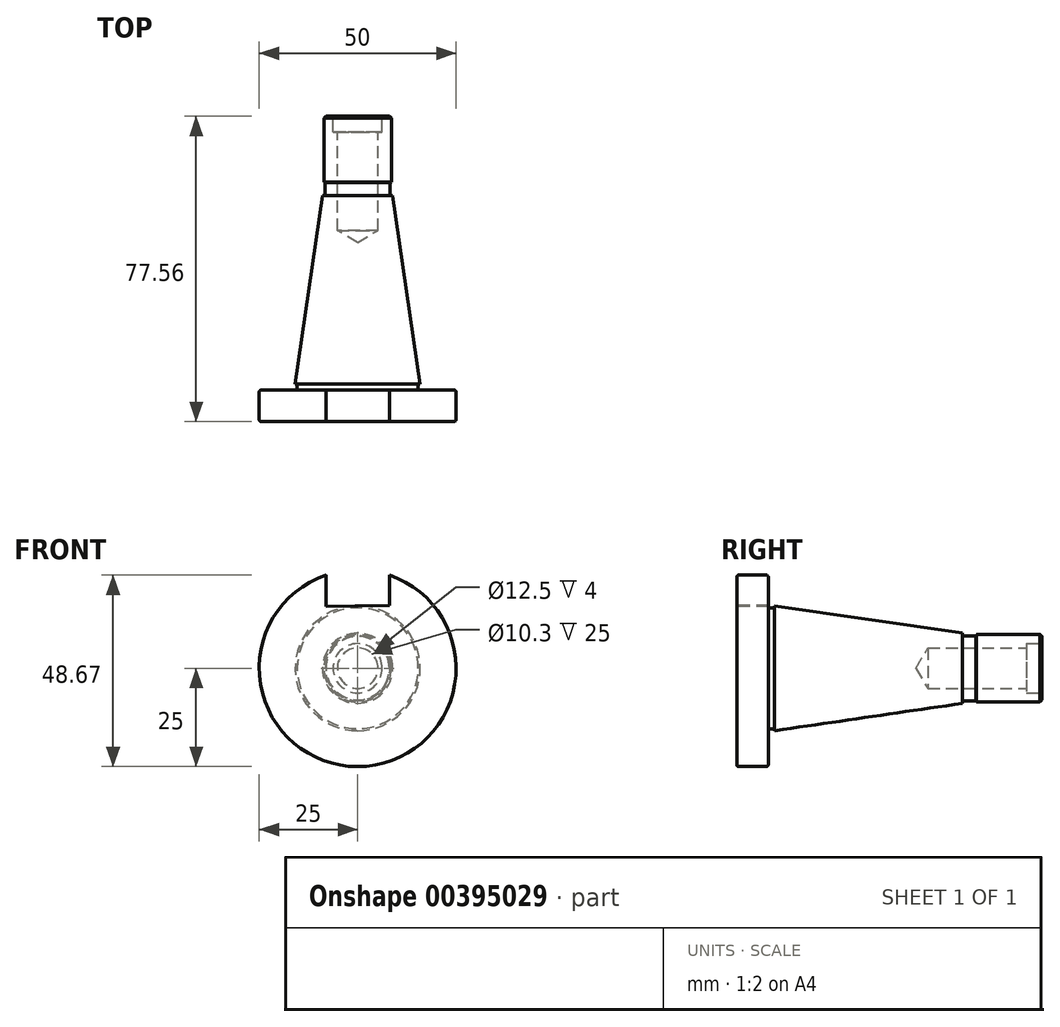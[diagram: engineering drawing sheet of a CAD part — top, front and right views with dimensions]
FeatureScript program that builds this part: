
annotation { "Feature Type Name" : "Feature", "Feature Type Description" : "" }
export const myFeature = defineFeature(function(context is Context, id is Id, definition is map)
    precondition{}
    {
        {
            var Q0;
            Q0=qCreatedBy(makeId("Right.planeOp"),FACE);
            var sketch = newSketch(context, id + "F0", { "sketchPlane" : qUnion([Q0])});
            skLineSegment(sketch, "E0", {"start": v(0, 0) * mm, "end": v(57.36, 0) * mm});
            skLineSegment(sketch, "E1", {"start": v(0, 0) * mm, "end": v(0, 25) * mm});
            skLineSegment(sketch, "E2", {"start": v(0, 25) * mm, "end": v(8, 25) * mm});
            skLineSegment(sketch, "E3", {"start": v(8, 25) * mm, "end": v(8, 15.88) * mm});
            skLineSegment(sketch, "E4", {"start": v(9.6, 15.88) * mm, "end": v(57.36, 8.9) * mm});
            skLineSegment(sketch, "E5", {"start": v(57.36, 8.9) * mm, "end": v(57.36, 0) * mm});
            skLineSegment(sketch, "E6", {"start": v(9.6, 15.88) * mm, "end": v(9.6, 15.38) * mm});
            skLineSegment(sketch, "E7", {"start": v(9.6, 15.38) * mm, "end": v(8, 15.38) * mm});
            skLineSegment(sketch, "E8", {"start": v(8, 15.38) * mm, "end": v(8, 15.88) * mm});
            skSolve(sketch);
        }
        {
            var Q0;
            Q0 = qSketchRegion(id + "F0", true);
            var Q1;
            Q1=sQuery(id+"F0.wireOp",EDGE,"E0");
            revolve(context, id + "F1", {"entities" : qUnion([Q0]), "axis" : qUnion([Q1]), "revolveType" : RevolveType.FULL});
        }
        {
            var Q0;
            Q0=makeQuery(id+"F1.opRevolve","SWEPT_FACE",FACE,{"disambiguationData":[OSD([sQuery(id+"F0.wireOp",EDGE,"E5")])]});
            var sketch = newSketch(context, id + "F2", { "sketchPlane" : qUnion([Q0])});
            skCircle(sketch, "E9", {"center": v(0, 0) * mm, "radius": 8.25 * mm});
            skSolve(sketch);
        }
        {
            var Q0;
            Q0 = qSketchRegion(id + "F2", true);
            extrude(context, id + "F3", {"entities" : qUnion([Q0]), "operationType" : NewBodyOperationType.ADD, "depth" : 3 * mm});
        }
        {
            var Q0;
            Q0=makeQuery(id+"F3.opExtrude","CAP_FACE",FACE,{"disambiguationData":[OSD([sQuery(id+"F2.wireOp",EDGE,"E9")])],"isStart":false});
            var sketch = newSketch(context, id + "F4", { "sketchPlane" : qUnion([Q0])});
            skCircle(sketch, "E10", {"center": v(0, 0) * mm, "radius": 8.55 * mm});
            skSolve(sketch);
        }
        {
            var Q0;
            Q0 = qSketchRegion(id + "F4", true);
            extrude(context, id + "F5", {"entities" : qUnion([Q0]), "operationType" : NewBodyOperationType.ADD, "depth" : 17.2 * mm});
        }
        {
            var Q0;
            Q0=makeQuery(id+"F5.opExtrude","CAP_FACE",FACE,{"disambiguationData":[OSD([sQuery(id+"F4.wireOp",EDGE,"E10")])],"isStart":false});
            var sketch = newSketch(context, id + "F6", { "sketchPlane" : qUnion([Q0])});
            skCircle(sketch, "E11", {"center": v(0, 0) * mm, "radius": 6.25 * mm});
            skSolve(sketch);
        }
        {
            var Q0;
            Q0=makeQuery(id+"F5.opExtrude","CAP_EDGE",EDGE,{"disambiguationData":[OSD([sQuery(id+"F4.wireOp",EDGE,"E10")])],"isStart":true});
            chamfer(context, id + "F7", {"entities" : qUnion([Q0]), "chamferType" : ChamferType.OFFSET_ANGLE, "width" : .5 * mm, "oppositeDirection" : false, "angle" : 75 * degree, "tangentPropagation" : true});
        }
        {
            var Q0;
            Q0 = qSketchRegion(id + "F6", true);
            extrude(context, id + "F8", {"entities" : qUnion([Q0]), "operationType" : NewBodyOperationType.REMOVE, "oppositeDirection" : true, "depth" : 4 * mm});
        }
        {
            var Q0;
            Q0=makeQuery(id+"F8.boolean.opBoolean","COPY",FACE,{"derivedFrom":makeQuery(id+"F8.opExtrude","CAP_FACE",FACE,{"disambiguationData":[OSD([sQuery(id+"F6.wireOp",EDGE,"E11")])],"isStart":false})});
            var sketch = newSketch(context, id + "F9", { "sketchPlane" : qUnion([Q0])});
            skPoint(sketch, "E12", {"position": v(0, 0) * mm});
            skSolve(sketch);
        }
        {
            var Q0;
            Q0=sQuery(id+"F9.wireOp",VERTEX,"E12");
            var Q1;
            Q1=makeQuery(id+"F1.opRevolve","SWEPT_BODY",BODY,{"disambiguationData":[OSD([sQuery(id+"F0.wireOp",EDGE,"E0"),sQuery(id+"F0.wireOp",EDGE,"E1"),sQuery(id+"F0.wireOp",EDGE,"E2"),sQuery(id+"F0.wireOp",EDGE,"E3"),sQuery(id+"F0.wireOp",EDGE,"E4"),sQuery(id+"F0.wireOp",EDGE,"E5")])]});
            hole(context, id + "F10", {"style" : HoleStyle.SIMPLE, "endStyle" : HoleEndStyle.BLIND, "standardTappedOrClearance" : lookupTablePath({ "standard" : "ISO", "engagement" : "75%", "pitch" : "1.75 mm", "size" : "M12", "type" : "Tapped" }), "standardBlindInLast" : lookupTablePath({ "standard" : "ISO", "engagement" : "75%", "pitch" : "1.75 mm", "size" : "M12", "type" : "Tapped" }), "holeDiameter" : 10.3 * mm, "showTappedDepth" : true, "holeDepth" : 25 * mm, "tappedDepth" : 21.5 * mm, "tapClearance" : 2, "locations" : qUnion([Q0]), "scope" : qUnion([Q1]), "majorDiameter" : 12 * mm});
        }
        {
            var Q0;
            Q0=makeQuery(id+"F1.opRevolve","SWEPT_FACE",FACE,{"disambiguationData":[OSD([sQuery(id+"F0.wireOp",EDGE,"E2")])]});
            fillet(context, id + "F11", {"entities" : qUnion([Q0]), "radius" : .5 * mm, "tangentPropagation" : true, "allowEdgeOverflow" : false});
        }
        {
            var Q0;
            Q0=makeQuery(id+"F5.opExtrude","CAP_EDGE",EDGE,{"disambiguationData":[OSD([sQuery(id+"F4.wireOp",EDGE,"E10")])],"isStart":false});
            var Q1;
            Q1=makeQuery(id+"F8.boolean.opBoolean","COPY",EDGE,{"derivedFrom":makeQuery(id+"F8.opExtrude","CAP_EDGE",EDGE,{"disambiguationData":[OSD([sQuery(id+"F6.wireOp",EDGE,"E11")])],"isStart":true})});
            var Q2;
            Q2=makeQuery(id+"F10.hole-0.boolean.opBoolean","COPY",EDGE,{"derivedFrom":makeQuery(id+"F10.hole-0.opRevolve","SWEPT_EDGE",EDGE,{"disambiguationData":[OSD([sQuery(id+"F10.hole-0.sketch.wireOp",EDGE,"core_line_2"),sQuery(id+"F10.hole-0.sketch.wireOp",EDGE,"core_line_3")])]})});
            chamfer(context, id + "F12", {"entities" : qUnion([Q0, Q1, Q2]), "width" : .5 * mm, "tangentPropagation" : true});
        }
        {
            var Q0;
            Q0=makeQuery(id+"F1.opRevolve","SWEPT_FACE",FACE,{"disambiguationData":[OSD([sQuery(id+"F0.wireOp",EDGE,"E1")])]});
            var sketch = newSketch(context, id + "F13", { "sketchPlane" : qUnion([Q0])});
            skCircle(sketch, "E13", {"center": v(0.27, 0) * mm, "radius": 15.88 * mm, "construction": true});
            skLineSegment(sketch, "E14", {"start": v(0, 15.87) * mm, "end": v(-8.05, 15.73) * mm});
            skLineSegment(sketch, "E15", {"start": v(-8.05, 15.73) * mm, "end": v(8.05, 16.01) * mm});
            skLineSegment(sketch, "E16", {"start": v(8.05, 16.01) * mm, "end": v(8.05, 25) * mm});
            skLineSegment(sketch, "E17", {"start": v(8.05, 25) * mm, "end": v(-8.05, 25) * mm});
            skLineSegment(sketch, "E18", {"start": v(-8.05, 25) * mm, "end": v(-8.05, 15.73) * mm});
            skLineSegment(sketch, "E19", {"start": v(0, 0) * mm, "end": v(0, 15.87) * mm, "construction": true});
            skPoint(sketch, "E20", {"position": v(0, 15.87) * mm});
            skSolve(sketch);
        }
        {
            var Q0;
            Q0 = qSketchRegion(id + "F13", true);
            var Q1;
            Q1=makeQuery(id+"F1.opRevolve","SWEPT_FACE",FACE,{"disambiguationData":[OSD([sQuery(id+"F0.wireOp",EDGE,"E3")])]});
            extrude(context, id + "F14", {"entities" : qUnion([Q0]), "operationType" : NewBodyOperationType.REMOVE, "endBound" : BoundingType.UP_TO_SURFACE, "oppositeDirection" : true, "endBoundEntityFace" : qUnion([Q1]), "depth" : 25 * mm});
        }
    });
